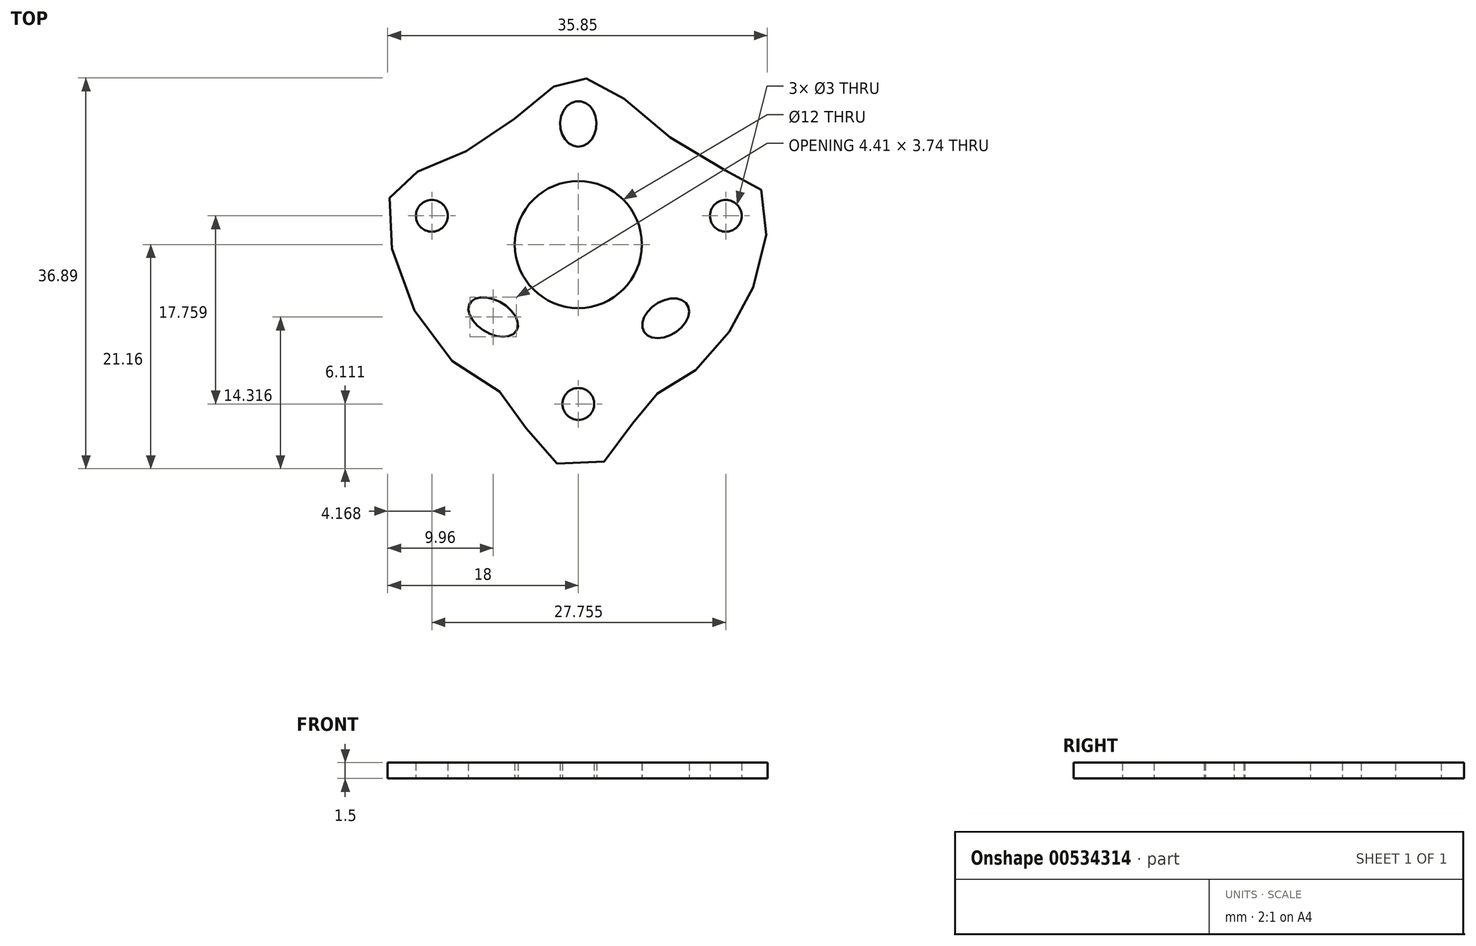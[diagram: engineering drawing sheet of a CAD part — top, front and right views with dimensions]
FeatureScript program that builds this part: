
annotation { "Feature Type Name" : "Feature", "Feature Type Description" : "" }
export const myFeature = defineFeature(function(context is Context, id is Id, definition is map)
    precondition{}
    {
        {
            var Q0;
            Q0=qCreatedBy(makeId("Top.planeOp"),FACE);
            var sketch = newSketch(context, id + "F0", { "sketchPlane" : qUnion([Q0])});
            skPoint(sketch, "E0", {"position": v(-6.76, 11.3) * mm});
            skPoint(sketch, "E1", {"position": v(-2.33, 14.92) * mm});
            skPoint(sketch, "E2", {"position": v(0, 15.73) * mm});
            skPoint(sketch, "E3", {"position": v(2.9, 14.82) * mm});
            skPoint(sketch, "E4", {"position": v(8.07, 10.55) * mm});
            skPoint(sketch, "E5", {"position": v(15.06, 6.46) * mm});
            skPoint(sketch, "E6", {"position": v(17.43, 4.91) * mm});
            skPoint(sketch, "E7", {"position": v(17.6, 0) * mm});
            skPoint(sketch, "E8", {"position": v(15.8, -5.62) * mm});
            skPoint(sketch, "E9", {"position": v(12.8, -10.07) * mm});
            skPoint(sketch, "E10", {"position": v(8.89, -13.43) * mm});
            skPoint(sketch, "E11", {"position": v(6.07, -14.98) * mm});
            skPoint(sketch, "E12", {"position": v(4.16, -18.89) * mm});
            skPoint(sketch, "E13", {"position": v(0, -21.16) * mm});
            skPoint(sketch, "E14", {"position": v(-4.16, -18.84) * mm});
            skPoint(sketch, "E15", {"position": v(-6.22, -14.9) * mm});
            skPoint(sketch, "E16", {"position": v(-11.24, -11.55) * mm});
            skPoint(sketch, "E17", {"position": v(-16.18, -4.71) * mm});
            skPoint(sketch, "E18", {"position": v(-18, 2.92) * mm});
            skPoint(sketch, "E19", {"position": v(-16.91, 5.91) * mm});
            skPoint(sketch, "E20", {"position": v(-12.73, 7.82) * mm});
            skPoint(sketch, "E21", {"position": v(13.92, 2.71) * mm});
            skPoint(sketch, "E22", {"position": v(-13.83, 2.71) * mm});
            skPoint(sketch, "E23", {"position": v(-8.04, -6.84) * mm});
            skPoint(sketch, "E24", {"position": v(8.25, -6.96) * mm});
            skPoint(sketch, "E25", {"position": v(0, -15.05) * mm});
            skPoint(sketch, "E26", {"position": v(0, 11.4) * mm});
            skFitSpline(sketch, "E27", {"points": [v(-2.33, 14.92) * mm, v(0, 15.73) * mm, v(2.9, 14.82) * mm, v(8.07, 10.55) * mm, v(15.06, 6.46) * mm, v(17.43, 4.91) * mm, v(17.6, 0) * mm, v(15.8, -5.62) * mm, v(12.8, -10.07) * mm, v(8.89, -13.43) * mm, v(6.07, -14.98) * mm, v(4.16, -18.89) * mm, v(0, -21.16) * mm, v(-4.16, -18.84) * mm, v(-6.22, -14.9) * mm, v(-11.24, -11.55) * mm, v(-16.18, -4.71) * mm, v(-18, 2.92) * mm, v(-16.91, 5.91) * mm, v(-12.73, 7.82) * mm, v(-6.76, 11.3) * mm, v(-2.33, 14.92) * mm]});
            skCircle(sketch, "E28", {"center": v(-13.83, 2.71) * mm, "radius": 1.5 * mm});
            skCircle(sketch, "E29", {"center": v(13.92, 2.71) * mm, "radius": 1.5 * mm});
            skCircle(sketch, "E30", {"center": v(0, -15.05) * mm, "radius": 1.5 * mm});
            skEllipse(sketch, "E31", {"center": v(-8.04, -6.84) * mm, "majorRadius": 2.56 * mm, "minorRadius": 1.55 * mm, "majorAxis": v(0.86, -0.5)});
            skEllipse(sketch, "E32", {"center": v(8.25, -6.96) * mm, "majorRadius": 2.42 * mm, "minorRadius": 1.61 * mm, "majorAxis": v(-0.84, -0.53)});
            skEllipse(sketch, "E33", {"center": v(0, 11.4) * mm, "majorRadius": 2.15 * mm, "minorRadius": 1.72 * mm, "majorAxis": v(0, -1)});
            skCircle(sketch, "E34", {"center": v(0, 0) * mm, "radius": 6 * mm});
            skSolve(sketch);
        }
        {
            var Q0;
            Q0=qSketchRegion(id+"F0",true);
            extrude(context, id + "F1", {"entities" : qUnion([Q0]), "depth" : 1.5 * mm});
        }
    });
